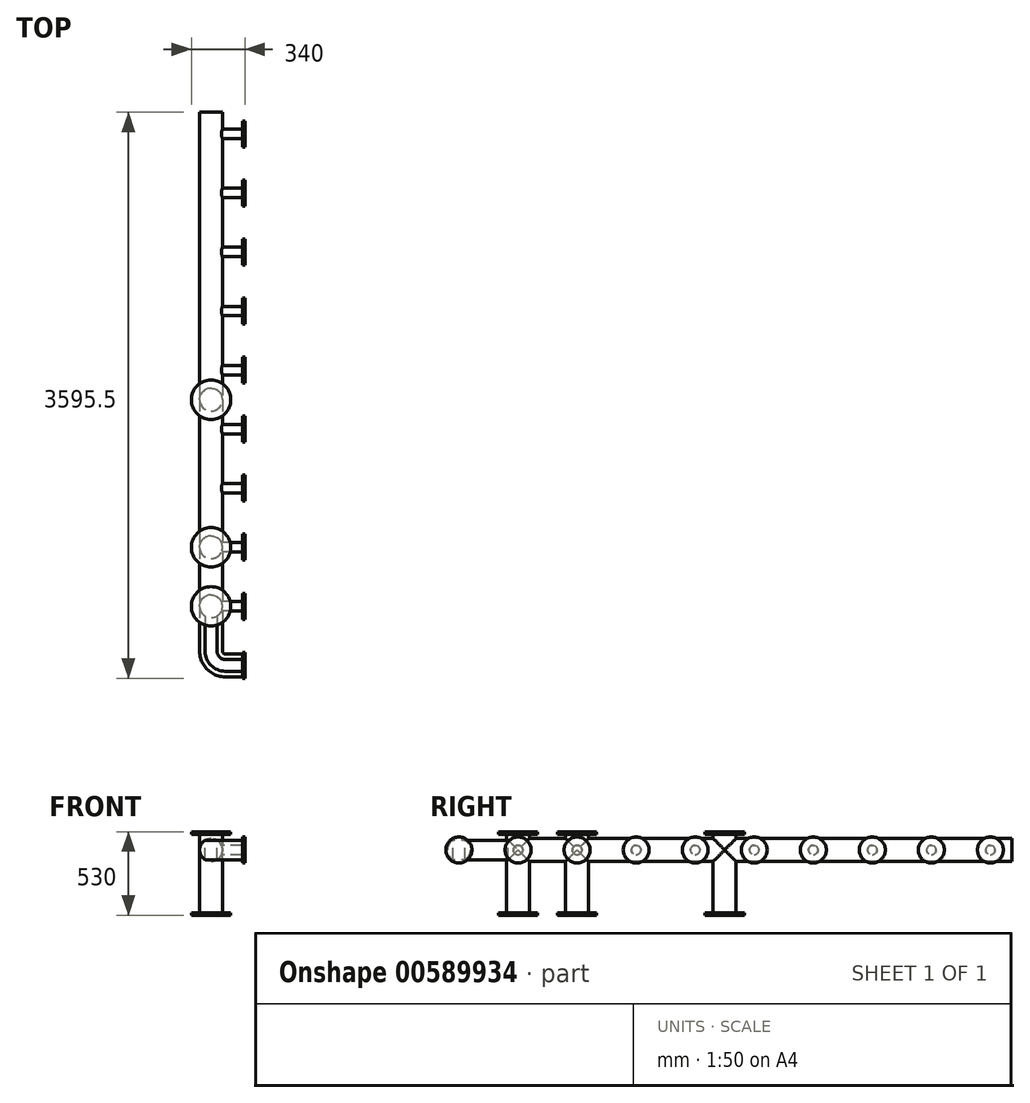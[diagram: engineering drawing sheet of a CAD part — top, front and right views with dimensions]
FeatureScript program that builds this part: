
annotation { "Feature Type Name" : "Feature", "Feature Type Description" : "" }
export const myFeature = defineFeature(function(context is Context, id is Id, definition is map)
    precondition{}
    {
        {
            var Q0;
            Q0=qCreatedBy(makeId("Front.planeOp"),FACE);
            var sketch = newSketch(context, id + "F0", { "sketchPlane" : qUnion([Q0])});
            skCircle(sketch, "E0", {"center": v(0, 0) * mm, "radius": 72.5 * mm});
            skSolve(sketch);
        }
        {
            var Q0;
            Q0=makeQuery(id+"F0.imprint","IMPRINT",FACE,{"disambiguationData":[TD([[makeQuery(id+"F0.imprint","IMPRINT",EDGE,{"derivedFrom":sQuery(id+"F0.wireOp",EDGE,"E0")}),1.0]])]});
            extrude(context, id + "F1", {"entities" : qUnion([Q0]), "oppositeDirection" : true, "depth" : 3200 * mm, "offsetDistance" : 25 * mm});
        }
        {
            var Q0;
            Q0=qCreatedBy(makeId("Right.planeOp"),FACE);
            var sketch = newSketch(context, id + "F2", { "sketchPlane" : qUnion([Q0])});
            skCircle(sketch, "E1", {"center": v(62.5, 0) * mm, "radius": 30 * mm});
            skCircle(sketch, "E2.1.0.0", {"center": v(437.5, 0) * mm, "radius": 30 * mm});
            skCircle(sketch, "E2.2.0.0", {"center": v(812.5, 0) * mm, "radius": 30 * mm});
            skCircle(sketch, "E2.3.0.0", {"center": v(1187.5, 0) * mm, "radius": 30 * mm});
            skCircle(sketch, "E2.4.0.0", {"center": v(1562.5, 0) * mm, "radius": 30 * mm});
            skCircle(sketch, "E2.5.0.0", {"center": v(1937.5, 0) * mm, "radius": 30 * mm});
            skCircle(sketch, "E2.6.0.0", {"center": v(2312.5, 0) * mm, "radius": 30 * mm});
            skCircle(sketch, "E2.7.0.0", {"center": v(2687.5, 0) * mm, "radius": 30 * mm});
            skCircle(sketch, "E2.8.0.0", {"center": v(3062.5, 0) * mm, "radius": 30 * mm});
            skLineSegment(sketch, "E2.direction1", {"start": v(62.5, 0) * mm, "end": v(437.5, 0) * mm, "construction": true});
            skSolve(sketch);
        }
        {
            var Q0;
            Q0 = qSketchRegion(id + "F2", true);
            extrude(context, id + "F3", {"entities" : qUnion([Q0]), "operationType" : NewBodyOperationType.ADD, "depth" : 215 * mm, "offsetDistance" : 25 * mm});
        }
        {
            var Q0;
            Q0=makeQuery(id+"F3.opExtrude","CAP_FACE",FACE,{"disambiguationData":[OSD([sQuery(id+"F2.wireOp",EDGE,"E1")])],"isStart":false});
            var sketch = newSketch(context, id + "F4", { "sketchPlane" : qUnion([Q0])});
            skCircle(sketch, "E3", {"center": v(62.5, 0) * mm, "radius": 82.5 * mm});
            skCircle(sketch, "E4.1.0.0", {"center": v(437.5, 0) * mm, "radius": 82.5 * mm});
            skCircle(sketch, "E4.2.0.0", {"center": v(812.5, 0) * mm, "radius": 82.5 * mm});
            skCircle(sketch, "E4.3.0.0", {"center": v(1187.5, 0) * mm, "radius": 82.5 * mm});
            skCircle(sketch, "E4.4.0.0", {"center": v(1562.5, 0) * mm, "radius": 82.5 * mm});
            skCircle(sketch, "E4.5.0.0", {"center": v(1937.5, 0) * mm, "radius": 82.5 * mm});
            skCircle(sketch, "E4.6.0.0", {"center": v(2312.5, 0) * mm, "radius": 82.5 * mm});
            skCircle(sketch, "E4.7.0.0", {"center": v(2687.5, 0) * mm, "radius": 82.5 * mm});
            skCircle(sketch, "E4.8.0.0", {"center": v(3062.5, 0) * mm, "radius": 82.5 * mm});
            skLineSegment(sketch, "E4.direction1", {"start": v(62.5, 0) * mm, "end": v(437.5, 0) * mm, "construction": true});
            skSolve(sketch);
        }
        {
            var Q0;
            Q0 = qSketchRegion(id + "F4", true);
            extrude(context, id + "F5", {"entities" : qUnion([Q0]), "operationType" : NewBodyOperationType.ADD, "oppositeDirection" : true, "depth" : 15 * mm, "offsetDistance" : 25 * mm});
        }
        {
            var Q0;
            Q0=qCreatedBy(makeId("Top.planeOp"),FACE);
            var sketch = newSketch(context, id + "F6", { "sketchPlane" : qUnion([Q0])});
            skCircle(sketch, "E5", {"center": v(0, 62) * mm, "radius": 72.5 * mm});
            skCircle(sketch, "E6.0.1.0", {"center": v(0, 437) * mm, "radius": 72.5 * mm});
            skLineSegment(sketch, "E6.direction1", {"start": v(0, 62) * mm, "end": v(25, 62) * mm, "construction": true});
            skLineSegment(sketch, "E6.direction2", {"start": v(0, 62) * mm, "end": v(0, 437) * mm, "construction": true});
            skSolve(sketch);
        }
        {
            var Q0;
            Q0 = qSketchRegion(id + "F6", true);
            extrude(context, id + "F7", {"entities" : qUnion([Q0]), "operationType" : NewBodyOperationType.ADD, "oppositeDirection" : true, "depth" : 400 * mm, "offsetDistance" : 25 * mm});
        }
        {
            var Q0;
            Q0=makeQuery(id+"F7.opExtrude","CAP_FACE",FACE,{"disambiguationData":[OSD([sQuery(id+"F6.wireOp",EDGE,"E5")])],"isStart":false});
            var sketch = newSketch(context, id + "F8", { "sketchPlane" : qUnion([Q0])});
            skCircle(sketch, "E7", {"center": v(0, -62) * mm, "radius": 125 * mm});
            skCircle(sketch, "E8.0.1.0", {"center": v(0, -437) * mm, "radius": 125 * mm});
            skLineSegment(sketch, "E8.direction1", {"start": v(0, -62) * mm, "end": v(25, -62) * mm, "construction": true});
            skLineSegment(sketch, "E8.direction2", {"start": v(0, -62) * mm, "end": v(0, -437) * mm, "construction": true});
            skSolve(sketch);
        }
        {
            var Q0;
            Q0 = qSketchRegion(id + "F8", true);
            extrude(context, id + "F9", {"entities" : qUnion([Q0]), "operationType" : NewBodyOperationType.ADD, "depth" : 15 * mm, "offsetDistance" : 25 * mm});
        }
        {
            var Q0;
            Q0=qCreatedBy(makeId("Top.planeOp"),FACE);
            var sketch = newSketch(context, id + "F10", { "sketchPlane" : qUnion([Q0])});
            skCircle(sketch, "E9", {"center": v(0, 1374.5) * mm, "radius": 72.5 * mm});
            skSolve(sketch);
        }
        {
            var Q0;
            Q0 = qSketchRegion(id + "F10", true);
            extrude(context, id + "F11", {"entities" : qUnion([Q0]), "operationType" : NewBodyOperationType.ADD, "oppositeDirection" : true, "depth" : 400 * mm, "offsetDistance" : 25 * mm});
        }
        {
            var Q0;
            Q0=makeQuery(id+"F11.opExtrude","CAP_FACE",FACE,{"disambiguationData":[OSD([sQuery(id+"F10.wireOp",EDGE,"E9")])],"isStart":false});
            var sketch = newSketch(context, id + "F12", { "sketchPlane" : qUnion([Q0])});
            skCircle(sketch, "E10", {"center": v(0, -1374.5) * mm, "radius": 125 * mm});
            skSolve(sketch);
        }
        {
            var Q0;
            Q0 = qSketchRegion(id + "F12", true);
            extrude(context, id + "F13", {"entities" : qUnion([Q0]), "operationType" : NewBodyOperationType.ADD, "depth" : 15 * mm, "offsetDistance" : 25 * mm});
        }
        {
            var Q0;
            Q0=qCreatedBy(makeId("Top.planeOp"),FACE);
            var sketch = newSketch(context, id + "F14", { "sketchPlane" : qUnion([Q0])});
            skCircle(sketch, "E11", {"center": v(0, 62) * mm, "radius": 72.5 * mm});
            skCircle(sketch, "E12.0.1.0", {"center": v(0, 437) * mm, "radius": 72.5 * mm});
            skLineSegment(sketch, "E12.direction1", {"start": v(0, 62) * mm, "end": v(25, 62) * mm, "construction": true});
            skLineSegment(sketch, "E12.direction2", {"start": v(0, 62) * mm, "end": v(0, 437) * mm, "construction": true});
            skCircle(sketch, "E13", {"center": v(0, 1374.5) * mm, "radius": 72.5 * mm});
            skSolve(sketch);
        }
        {
            var Q0;
            Q0 = qSketchRegion(id + "F14", true);
            extrude(context, id + "F15", {"entities" : qUnion([Q0]), "operationType" : NewBodyOperationType.ADD, "depth" : 100 * mm, "offsetDistance" : 25 * mm});
        }
        {
            var Q0;
            Q0=makeQuery(id+"F15.opExtrude","CAP_FACE",FACE,{"disambiguationData":[OSD([sQuery(id+"F14.wireOp",EDGE,"E11")])],"isStart":false});
            var sketch = newSketch(context, id + "F16", { "sketchPlane" : qUnion([Q0])});
            skCircle(sketch, "E14", {"center": v(0, 62) * mm, "radius": 125 * mm});
            skCircle(sketch, "E15", {"center": v(0, 437) * mm, "radius": 125 * mm});
            skCircle(sketch, "E16", {"center": v(0, 1374) * mm, "radius": 125 * mm});
            skSolve(sketch);
        }
        {
            var Q0;
            Q0 = qSketchRegion(id + "F16", true);
            extrude(context, id + "F17", {"entities" : qUnion([Q0]), "operationType" : NewBodyOperationType.ADD, "depth" : 15 * mm, "offsetDistance" : 25 * mm});
        }
        {
            var Q0;
            Q0=qCreatedBy(makeId("Top.planeOp"),FACE);
            var sketch = newSketch(context, id + "F18", { "sketchPlane" : qUnion([Q0])});
            skLineSegment(sketch, "E17", {"start": v(0, 0) * mm, "end": v(0, -223) * mm});
            skLineSegment(sketch, "E18", {"start": v(90, -313) * mm, "end": v(200, -313) * mm});
            skPoint(sketch, "E19.visualSharp", {"position": v(0, -313) * mm});
            skArc(sketch, "E19.filletArc", {"start": v(0, -223) * mm, "mid": v(26.36, -286.64) * mm, "end": v(90, -313) * mm});
            skSolve(sketch);
        }
        {
            var Q0;
            Q0=makeQuery(id+"F1.opExtrude","CAP_FACE",FACE,{"disambiguationData":[OSD([sQuery(id+"F0.wireOp",EDGE,"E0")])],"isStart":true});
            var Q1;
            Q1=sQuery(id+"F18.wireOp",EDGE,"E17");
            var Q2;
            Q2=sQuery(id+"F18.wireOp",EDGE,"E19.filletArc");
            var Q3;
            Q3=sQuery(id+"F18.wireOp",EDGE,"E18");
            sweep(context, id + "F19", {"operationType" : NewBodyOperationType.ADD, "profiles" : qUnion([Q0]), "path" : qUnion([Q1, Q2, Q3])});
        }
        {
            var Q0;
            Q0=makeQuery(id+"F19.opSweep","CAP_FACE",FACE,{"disambiguationData":[OSD([sQuery(id+"F0.wireOp",EDGE,"E0"),sQuery(id+"F18.wireOp",VERTEX,"E18.end")])],"isStart":false});
            var sketch = newSketch(context, id + "F20", { "sketchPlane" : qUnion([Q0])});
            skCircle(sketch, "E20", {"center": v(-313, 0) * mm, "radius": 82.5 * mm});
            skSolve(sketch);
        }
        {
            var Q0;
            Q0 = qSketchRegion(id + "F20", true);
            extrude(context, id + "F21", {"entities" : qUnion([Q0]), "operationType" : NewBodyOperationType.ADD, "depth" : 15 * mm, "offsetDistance" : 25 * mm});
        }
    });
